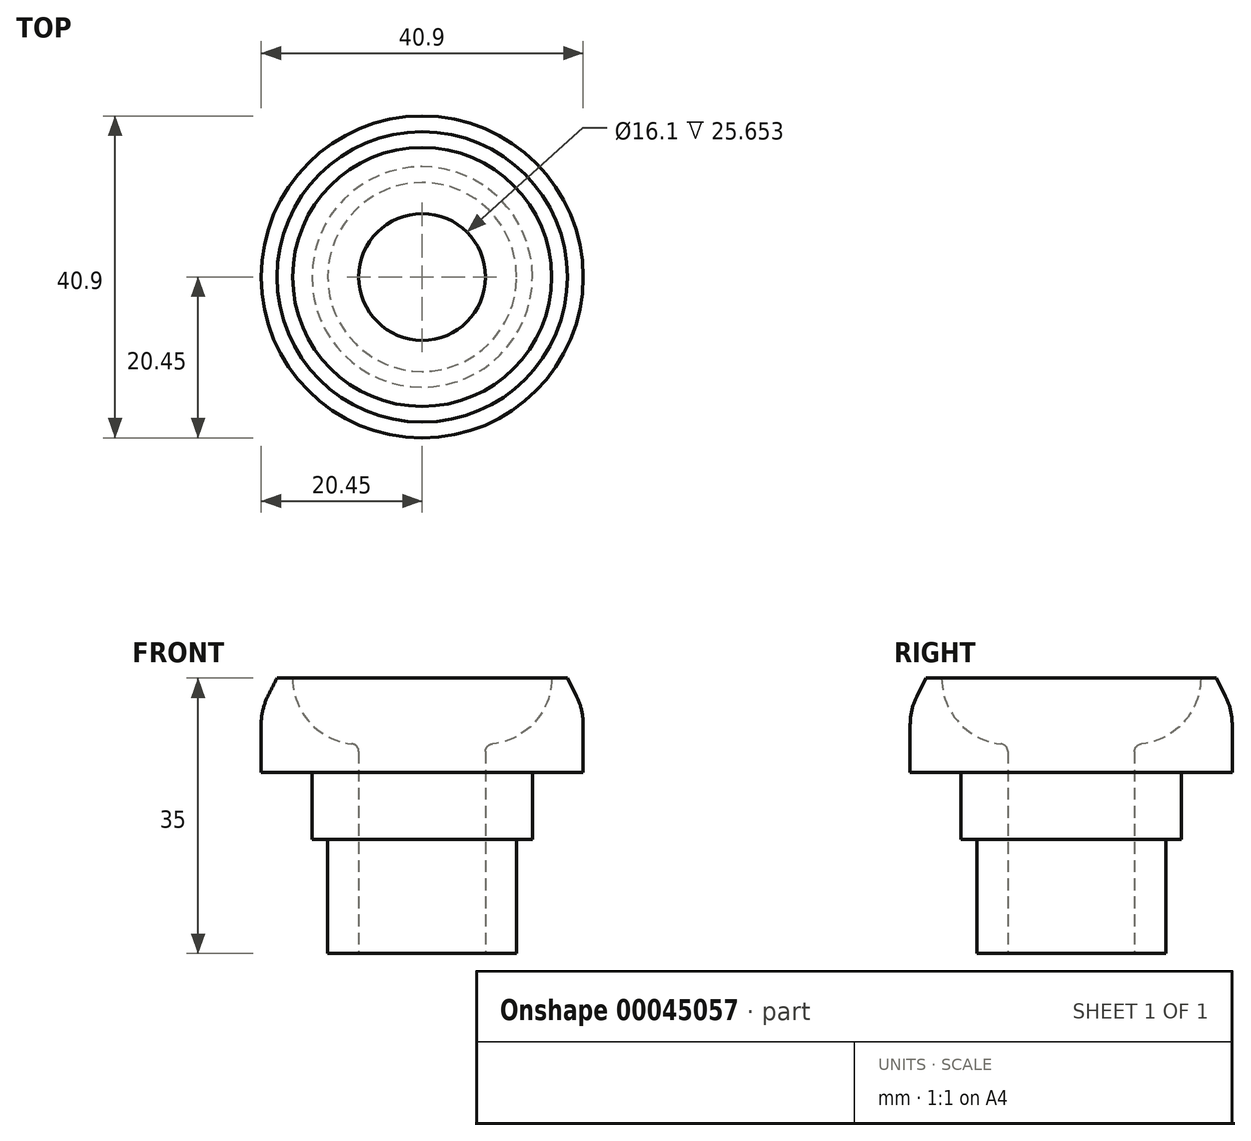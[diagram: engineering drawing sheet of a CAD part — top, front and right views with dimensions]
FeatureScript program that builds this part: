
annotation { "Feature Type Name" : "Feature", "Feature Type Description" : "" }
export const myFeature = defineFeature(function(context is Context, id is Id, definition is map)
    precondition{}
    {
        {
            var Q0;
            Q0=qCreatedBy(makeId("Front.planeOp"),FACE);
            var sketch = newSketch(context, id + "F0", { "sketchPlane" : qUnion([Q0])});
            skLineSegment(sketch, "E0", {"start": v(0, 0) * mm, "end": v(0, 35) * mm, "construction": true});
            skLineSegment(sketch, "E1", {"start": v(8.05, 0) * mm, "end": v(8.05, 25.65) * mm});
            skLineSegment(sketch, "E2", {"start": v(8.05, 0) * mm, "end": v(12, 0) * mm});
            skLineSegment(sketch, "E3", {"start": v(12, 0) * mm, "end": v(12, 14.5) * mm});
            skLineSegment(sketch, "E4", {"start": v(12, 14.5) * mm, "end": v(14, 14.5) * mm});
            skLineSegment(sketch, "E5", {"start": v(14, 14.5) * mm, "end": v(14, 23) * mm});
            skLineSegment(sketch, "E6", {"start": v(14, 23) * mm, "end": v(20.45, 23) * mm});
            skLineSegment(sketch, "E7", {"start": v(20.45, 23) * mm, "end": v(20.45, 29.11) * mm});
            skLineSegment(sketch, "E8", {"start": v(19.6, 32.69) * mm, "end": v(18.45, 35) * mm});
            skLineSegment(sketch, "E9", {"start": v(18.45, 35) * mm, "end": v(16.45, 35) * mm});
            skArc(sketch, "E10", {"start": v(8.94, 26.65) * mm, "mid": v(14.3, 29.39) * mm, "end": v(16.45, 35) * mm});
            skPoint(sketch, "E11.visualSharp", {"position": v(20.45, 31) * mm});
            skArc(sketch, "E11.filletArc", {"start": v(20.45, 29.11) * mm, "mid": v(20.24, 30.95) * mm, "end": v(19.6, 32.69) * mm});
            skPoint(sketch, "E12.visualSharp", {"position": v(8.05, 26.6) * mm});
            skArc(sketch, "E12.filletArc", {"start": v(8.94, 26.65) * mm, "mid": v(8.3, 26.32) * mm, "end": v(8.05, 25.65) * mm});
            skSolve(sketch);
        }
        {
            var Q0;
            Q0 = qSketchRegion(id + "F0", true);
            var Q1;
            Q1=sQuery(id+"F0.wireOp",EDGE,"E0");
            revolve(context, id + "F1", {"entities" : qUnion([Q0]), "axis" : qUnion([Q1]), "revolveType" : RevolveType.FULL});
        }
    });
